# Revit family: FS1790
name_source: partatom
category: Plumbing Fixtures
revit_build: Autodesk Revit 2017 (Build: 20190508_0315(x64)
units: mm (PartAtom-declared; Revit-internal decimal feet)

## family parameters
Cut with Voids When Loaded = No
Host = Face
Part Type = Normal
Room Calculation Point = No
Round Connector Dimension = Use Radius
Shared = No

## types (4) — shared parameters
Body Height = 1' - 5"
Default Elevation = 0' - 0"
Description = 24" x 24” x 17" DEEP FLOOR SINK
Floor Drain Material = Paint - Sherwin Williams Paint - #952C2A - Bellwood Red
Manufacturer = MIFAB
Model = FS1790
Top Length = 2' - 0"
Top Width = 2' - 0"
URL = WWW.MIFAB.COM
zero-valued in all types: CWFU, WFU

## per-type parameters (varying)
| type | Pipe Diameter | Pipe Radius |
| 4" Dia | 0' - 4" | 0' - 2" |
| 3" Dia | 0' - 3" | 0' - 1 1/2" |
| 2" Dia | 0' - 2" | 0' - 1" |
| 6" Dia | 0' - 6" | 0' - 3" |

## geometry (parser evidence)
native form markers: Blend x9, Sweep x5
no freeform markers — native parametric forms only
